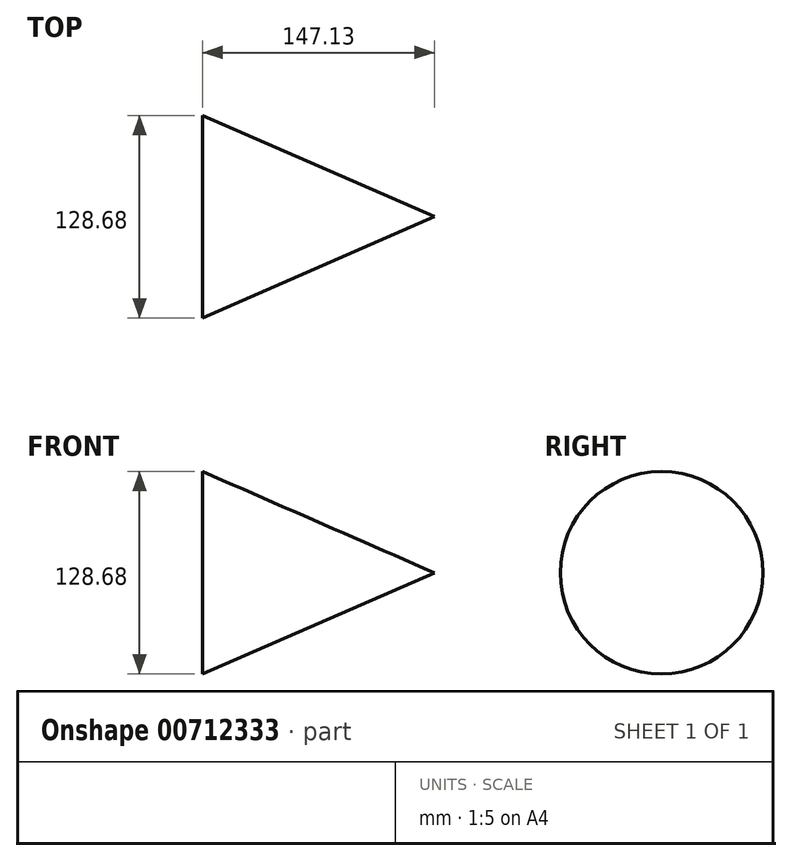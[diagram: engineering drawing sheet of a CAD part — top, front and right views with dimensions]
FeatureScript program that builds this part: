
annotation { "Feature Type Name" : "Feature", "Feature Type Description" : "" }
export const myFeature = defineFeature(function(context is Context, id is Id, definition is map)
    precondition{}
    {
        {
            var Q0;
            Q0=qCreatedBy(makeId("Front.planeOp"),FACE);
            var sketch = newSketch(context, id + "F0", { "sketchPlane" : qUnion([Q0])});
            skLineSegment(sketch, "E0", {"start": v(0, 64.34) * mm, "end": v(147.13, 0) * mm});
            skLineSegment(sketch, "E1", {"start": v(147.13, 0) * mm, "end": v(0, 0) * mm});
            skLineSegment(sketch, "E2", {"start": v(0, 0) * mm, "end": v(0, 64.34) * mm});
            skSolve(sketch);
        }
        {
            var Q0;
            Q0 = qSketchRegion(id + "F0", true);
            var Q1;
            Q1=sQuery(id+"F0.wireOp",EDGE,"E1");
            revolve(context, id + "F1", {"surfaceOperationType" : NewSurfaceOperationType.NEW, "entities" : qUnion([Q0]), "axis" : qUnion([Q1]), "revolveType" : RevolveType.FULL});
        }
    });
